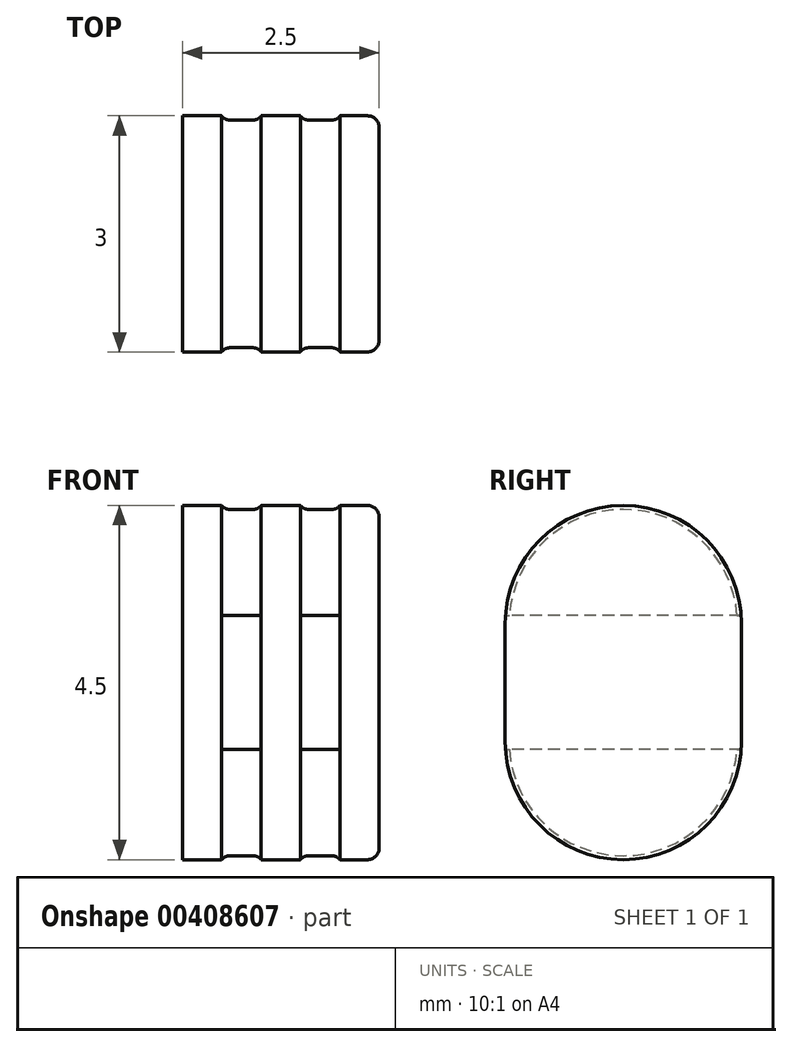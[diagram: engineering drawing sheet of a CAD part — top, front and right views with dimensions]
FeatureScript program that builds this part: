
annotation { "Feature Type Name" : "Feature", "Feature Type Description" : "" }
export const myFeature = defineFeature(function(context is Context, id is Id, definition is map)
    precondition{}
    {
        {
            var Q0;
            Q0=qCreatedBy(makeId("Right.planeOp"),FACE);
            var sketch = newSketch(context, id + "F0", { "sketchPlane" : qUnion([Q0])});
            skLineSegment(sketch, "E0", {"start": v(0, 0) * mm, "end": v(-1.5, 0) * mm});
            skLineSegment(sketch, "E1", {"start": v(0, 0) * mm, "end": v(0, 0.75) * mm});
            skLineSegment(sketch, "E2", {"start": v(-1.5, 0) * mm, "end": v(-1.5, 0.75) * mm});
            skEllipticalArc(sketch, "E3", {});
            skLineSegment(sketch, "E4", {"start": v(1.5, 0.75) * mm, "end": v(1.5, 0) * mm});
            skPoint(sketch, "E5.orphan", {"position": v(0, 2.25) * mm});
            skPoint(sketch, "E6.endSnap0", {"position": v(-0.75, 0) * mm});
            skEllipticalArc(sketch, "E7.MirrorCS", {});
            skLineSegment(sketch, "E8.MirrorCS", {"start": v(-1.5, 0) * mm, "end": v(-1.5, -0.75) * mm});
            skLineSegment(sketch, "E9.MirrorCS", {"start": v(1.5, -0.75) * mm, "end": v(1.5, 0) * mm});
            skLineSegment(sketch, "E10", {"start": v(0, 2.25) * mm, "end": v(0, -2.25) * mm});
            const initialGuessF0  = {"E3": [0, 0.00075, 0, 1, 0.0015, 0.0015, 4.71238898038469, 1.5707963267948966], "E7.MirrorCS": [0, -0.00075, 0, -1, 0.0015, 0.0015, 4.71238898038469, 1.5707963267948966]};
            skSetInitialGuess(sketch, initialGuessF0);
            skSolve(sketch);
        }
        {
            var Q0;
            {var subQ5=sQuery(id+"F0.wireOp",EDGE,"E0");Q0=makeQuery(id+"F0.imprint","IMPRINT",FACE,{"disambiguationData":[TD([[makeQuery(id+"F0.imprint","IMPRINT",EDGE,{"derivedFrom":subQ5}),-1.0]])]});}
            var Q1;
            {var subQ4=sQuery(id+"F0.wireOp",EDGE,"E4");Q1=makeQuery(id+"F0.imprint","IMPRINT",FACE,{"disambiguationData":[TD([[makeQuery(id+"F0.imprint","IMPRINT",EDGE,{"derivedFrom":subQ4}),-1.0]])]});}
            var Q2;
            {var subQ0=sQuery(id+"F0.wireOp",EDGE,"E0");Q2=makeQuery(id+"F0.imprint","IMPRINT",FACE,{"disambiguationData":[TD([[makeQuery(id+"F0.imprint","IMPRINT",EDGE,{"derivedFrom":subQ0}),1.0]])]});}
            extrude(context, id + "F1", {"entities" : qUnion([Q0, Q1, Q2]), "depth" : 2.5 * mm});
        }
        {
            var Q0;
            Q0=qCreatedBy(makeId("Right.planeOp"),FACE);
            cPlane(context, id + "F2", {"entities" : qUnion([Q0]), "cplaneType" : CPlaneType.OFFSET, "offset" : .5 * mm, "width" : 150 * mm, "height" : 150 * mm});
        }
        {
            var Q0;
            Q0=qCreatedBy(id+"F2.planeOp",FACE);
            var sketch = newSketch(context, id + "F3", { "sketchPlane" : qUnion([Q0])});
            skLineSegment(sketch, "E11", {"start": v(0, 0) * mm, "end": v(1.45, 0) * mm});
            skLineSegment(sketch, "E12", {"start": v(1.45, 0) * mm, "end": v(1.45, 0.75) * mm});
            skLineSegment(sketch, "E13", {"start": v(0, 0) * mm, "end": v(0, 2.2) * mm});
            skLineSegment(sketch, "E14", {"start": v(1.45, 0.75) * mm, "end": v(0, 0.75) * mm});
            skEllipticalArc(sketch, "E15", {});
            skLineSegment(sketch, "E16", {"start": v(-1.45, 0.75) * mm, "end": v(-1.45, -0.75) * mm});
            skLineSegment(sketch, "E17", {"start": v(-1.45, -0.75) * mm, "end": v(0, -0.75) * mm});
            skLineSegment(sketch, "E18", {"start": v(0, 0) * mm, "end": v(0, -2.2) * mm});
            skEllipticalArc(sketch, "E19", {});
            skLineSegment(sketch, "E20", {"start": v(1.45, 0) * mm, "end": v(1.45, -0.75) * mm});
            skCircle(sketch, "E21", {"center": v(0, 0) * mm, "radius": 3.08 * mm});
            const initialGuessF3  = {"E15": [0, 0.00075, 0, 1, 0.00145, 0.00145, 4.71238898038469, 1.5707963267948966], "E19": [0, -0.00075, 0, -1, 0.00145, 0.00145, 4.71238898038469, 1.5707963267948966]};
            skSetInitialGuess(sketch, initialGuessF3);
            skSolve(sketch);
        }
        {
            var Q0;
            Q0 = qSketchRegion(id + "F3", true);
            extrude(context, id + "F4", {"entities" : qUnion([Q0]), "operationType" : NewBodyOperationType.REMOVE, "depth" : .5 * mm});
        }
        {
            var Q0;
            Q0=qCreatedBy(id+"F2.planeOp",FACE);
            cPlane(context, id + "F5", {"entities" : qUnion([Q0]), "cplaneType" : CPlaneType.OFFSET, "offset" : 1 * mm, "width" : 150 * mm, "height" : 150 * mm});
        }
        {
            var Q0;
            Q0=qCreatedBy(id+"F5.planeOp",FACE);
            var sketch = newSketch(context, id + "F6", { "sketchPlane" : qUnion([Q0])});
            skLineSegment(sketch, "E22", {"start": v(0, 0) * mm, "end": v(1.45, 0) * mm});
            skLineSegment(sketch, "E23", {"start": v(1.45, 0) * mm, "end": v(1.45, 0.75) * mm});
            skLineSegment(sketch, "E24", {"start": v(0, 0) * mm, "end": v(0, 2.2) * mm});
            skLineSegment(sketch, "E25", {"start": v(1.45, 0.75) * mm, "end": v(0, 0.75) * mm});
            skEllipticalArc(sketch, "E26", {});
            skEllipticalArc(sketch, "E27.MirrorCS", {});
            skLineSegment(sketch, "E28.MirrorCS", {"start": v(1.45, 0) * mm, "end": v(1.45, -0.75) * mm});
            skEllipticalArc(sketch, "E29.MirrorCS", {});
            skLineSegment(sketch, "E30.MirrorCS", {"start": v(-1.45, 0) * mm, "end": v(-1.45, 0.75) * mm});
            skLineSegment(sketch, "E31.MirrorCS", {"start": v(-1.45, 0) * mm, "end": v(-1.45, -0.75) * mm});
            skEllipticalArc(sketch, "E32.MirrorCS", {});
            skCircle(sketch, "E33", {"center": v(0, 0) * mm, "radius": 2.92 * mm});
            const initialGuessF6  = {"E26": [0, 0.00075, 0, 1, 0.00145, 0.00145, 4.71238898038469, 0], "E27.MirrorCS": [0, -0.00075, 0, -1, 0.00145, 0.00145, 0, 1.5707963267948966], "E29.MirrorCS": [0, 0.00075, 0, 1, 0.00145, 0.00145, 0, 1.5707963267948966], "E32.MirrorCS": [0, -0.00075, 0, -1, 0.00145, 0.00145, 4.71238898038469, 0]};
            skSetInitialGuess(sketch, initialGuessF6);
            skSolve(sketch);
        }
        {
            var Q0;
            Q0=makeQuery(id+"F6.imprint","IMPRINT",FACE,{"disambiguationData":[TD([[makeQuery(id+"F6.imprint","IMPRINT",EDGE,{"derivedFrom":sQuery(id+"F6.wireOp",EDGE,"E23")}),-1.0]])]});
            extrude(context, id + "F7", {"entities" : qUnion([Q0]), "operationType" : NewBodyOperationType.REMOVE, "depth" : .5 * mm});
        }
        {
            var Q0;
            Q0=makeQuery(id+"F7.boolean.opBoolean","COPY",EDGE,{"derivedFrom":makeQuery(id+"F7.opExtrude","CAP_EDGE",EDGE,{"disambiguationData":[OSD([sQuery(id+"F6.wireOp",EDGE,"E26"),sQuery(id+"F6.wireOp",EDGE,"E29.MirrorCS")])],"isStart":false})});
            fillet(context, id + "F8", {"entities" : qUnion([Q0]), "radius" : .125 * mm, "tangentPropagation" : true, "allowEdgeOverflow" : false});
        }
        {
            var Q0;
            Q0=makeQuery(id+"F7.boolean.opBoolean","COPY",EDGE,{"derivedFrom":makeQuery(id+"F7.opExtrude","CAP_EDGE",EDGE,{"disambiguationData":[OSD([sQuery(id+"F6.wireOp",EDGE,"E26"),sQuery(id+"F6.wireOp",EDGE,"E29.MirrorCS")])],"isStart":true})});
            var Q1;
            Q1=makeQuery(id+"F4.boolean.opBoolean","COPY",EDGE,{"derivedFrom":makeQuery(id+"F4.opExtrude","CAP_EDGE",EDGE,{"disambiguationData":[OSD([sQuery(id+"F3.wireOp",EDGE,"E15")])],"isStart":false})});
            var Q2;
            Q2=makeQuery(id+"F4.boolean.opBoolean","COPY",EDGE,{"derivedFrom":makeQuery(id+"F4.opExtrude","CAP_EDGE",EDGE,{"disambiguationData":[OSD([sQuery(id+"F3.wireOp",EDGE,"E15")])],"isStart":true})});
            var Q3;
            Q3=makeQuery(id+"F4.boolean.opBoolean","COPY",EDGE,{"derivedFrom":makeQuery(id+"F4.opExtrude","CAP_EDGE",EDGE,{"disambiguationData":[OSD([sQuery(id+"F3.wireOp",EDGE,"E19")])],"isStart":true})});
            var Q4;
            Q4=makeQuery(id+"F4.boolean.opBoolean","COPY",EDGE,{"derivedFrom":makeQuery(id+"F4.opExtrude","CAP_EDGE",EDGE,{"disambiguationData":[OSD([sQuery(id+"F3.wireOp",EDGE,"E19")])],"isStart":false})});
            var Q5;
            Q5=makeQuery(id+"F7.boolean.opBoolean","COPY",EDGE,{"derivedFrom":makeQuery(id+"F7.opExtrude","CAP_EDGE",EDGE,{"disambiguationData":[OSD([sQuery(id+"F6.wireOp",EDGE,"E27.MirrorCS"),sQuery(id+"F6.wireOp",EDGE,"E32.MirrorCS")])],"isStart":true})});
            fillet(context, id + "F9", {"entities" : qUnion([Q0, Q1, Q2, Q3, Q4, Q5]), "radius" : .125 * mm, "tangentPropagation" : true, "allowEdgeOverflow" : false});
        }
        {
            var Q0;
            Q0=makeQuery(id+"F1.opExtrude","CAP_EDGE",EDGE,{"disambiguationData":[OSD([sQuery(id+"F0.wireOp",EDGE,"E3")])],"isStart":false});
            var Q1;
            Q1=makeQuery(id+"F1.opExtrude","CAP_EDGE",EDGE,{"disambiguationData":[OSD([sQuery(id+"F0.wireOp",EDGE,"E4"),sQuery(id+"F0.wireOp",EDGE,"E9.MirrorCS")])],"isStart":false});
            var Q2;
            Q2=makeQuery(id+"F1.opExtrude","CAP_EDGE",EDGE,{"disambiguationData":[OSD([sQuery(id+"F0.wireOp",EDGE,"E7.MirrorCS")])],"isStart":false});
            var Q3;
            Q3=makeQuery(id+"F1.opExtrude","CAP_EDGE",EDGE,{"disambiguationData":[OSD([sQuery(id+"F0.wireOp",EDGE,"E2"),sQuery(id+"F0.wireOp",EDGE,"E8.MirrorCS")])],"isStart":false});
            fillet(context, id + "F10", {"entities" : qUnion([Q0, Q1, Q2, Q3]), "radius" : .15 * mm, "tangentPropagation" : true, "allowEdgeOverflow" : false});
        }
        {
            var Q0;
            Q0=qCreatedBy(makeId("Front.planeOp"),FACE);
            var sketch = newSketch(context, id + "F11", { "sketchPlane" : qUnion([Q0])});
            skLineSegment(sketch, "E34", {"start": v(0, 0) * mm, "end": v(0.75, 0) * mm});
            skLineSegment(sketch, "E35", {"start": v(0.75, 0.85) * mm, "end": v(1, 0.85) * mm});
            skLineSegment(sketch, "E36", {"start": v(0.75, -0.85) * mm, "end": v(0.5, -0.85) * mm});
            skLineSegment(sketch, "E37.bottom", {"start": v(1, 0.85) * mm, "end": v(0.5, 0.85) * mm});
            skLineSegment(sketch, "E37.top", {"start": v(1, -0.85) * mm, "end": v(0.5, -0.85) * mm});
            skLineSegment(sketch, "E37.left", {"start": v(1, 0.85) * mm, "end": v(1, -0.85) * mm});
            skLineSegment(sketch, "E37.right", {"start": v(0.5, 0.85) * mm, "end": v(0.5, -0.85) * mm});
            skLineSegment(sketch, "E38", {"start": v(0, 0) * mm, "end": v(1.25, 0) * mm});
            skLineSegment(sketch, "E39", {"start": v(1.25, 0) * mm, "end": v(1.25, 1.35) * mm});
            skLineSegment(sketch, "E40.MirrorCS", {"start": v(1.5, -0.85) * mm, "end": v(2, -0.85) * mm});
            skLineSegment(sketch, "E41.MirrorCS", {"start": v(1.5, 0.85) * mm, "end": v(1.5, -0.85) * mm});
            skLineSegment(sketch, "E42.MirrorCS", {"start": v(2, 0.85) * mm, "end": v(2, -0.85) * mm});
            skLineSegment(sketch, "E43.MirrorCS", {"start": v(1.75, 0.85) * mm, "end": v(1.5, 0.85) * mm});
            skLineSegment(sketch, "E44.MirrorCS", {"start": v(1.5, 0.85) * mm, "end": v(2, 0.85) * mm});
            skSolve(sketch);
        }
        {
            var Q0;
            Q0 = qSketchRegion(id + "F11", true);
            extrude(context, id + "F12", {"entities" : qUnion([Q0]), "operationType" : NewBodyOperationType.REMOVE, "endBound" : BoundingType.THROUGH_ALL, "oppositeDirection" : true, "depth" : 25 * mm, "hasSecondDirection" : true, "secondDirectionOppositeDirection" : false, "secondDirectionDepth" : 25 * mm});
        }
    });
